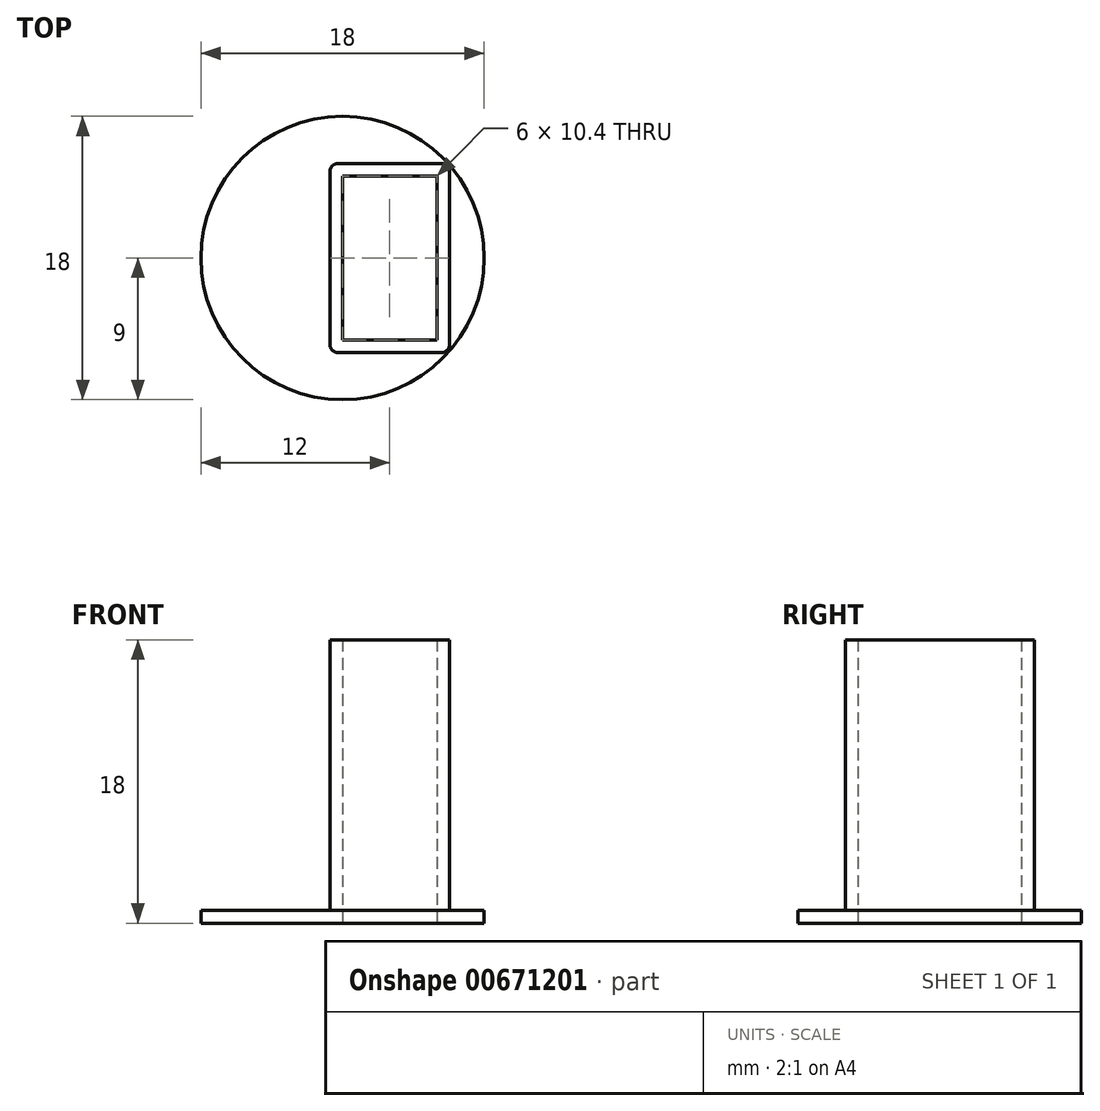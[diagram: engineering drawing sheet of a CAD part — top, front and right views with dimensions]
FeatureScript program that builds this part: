
annotation { "Feature Type Name" : "Feature", "Feature Type Description" : "" }
export const myFeature = defineFeature(function(context is Context, id is Id, definition is map)
    precondition{}
    {
        {
            var Q0;
            Q0=qCreatedBy(makeId("Top.planeOp"),FACE);
            var sketch = newSketch(context, id + "F0", { "sketchPlane" : qUnion([Q0])});
            skCircle(sketch, "E0", {"center": v(0, 0) * mm, "radius": 9 * mm});
            skLineSegment(sketch, "E1.bottom", {"start": v(0, 5.2) * mm, "end": v(6, 5.2) * mm});
            skLineSegment(sketch, "E1.top", {"start": v(0, -5.2) * mm, "end": v(6, -5.2) * mm});
            skLineSegment(sketch, "E1.left", {"start": v(0, 5.2) * mm, "end": v(0, -5.2) * mm});
            skLineSegment(sketch, "E1.right", {"start": v(6, 5.2) * mm, "end": v(6, -5.2) * mm});
            skLineSegment(sketch, "E2.0", {"start": v(6.8, 5.5) * mm, "end": v(6.8, -5.5) * mm});
            skLineSegment(sketch, "E2.1", {"start": v(-0.3, 6) * mm, "end": v(6.3, 6) * mm});
            skLineSegment(sketch, "E2.2", {"start": v(-0.8, 5.5) * mm, "end": v(-0.8, -5.5) * mm});
            skLineSegment(sketch, "E2.3", {"start": v(-0.3, -6) * mm, "end": v(6.3, -6) * mm});
            skPoint(sketch, "E3.visualSharp", {"position": v(-0.8, 6) * mm});
            skArc(sketch, "E3.filletArc", {"start": v(-0.3, 6) * mm, "mid": v(-0.65, 5.85) * mm, "end": v(-0.8, 5.5) * mm});
            skPoint(sketch, "E4.visualSharp", {"position": v(-0.8, -6) * mm});
            skArc(sketch, "E4.filletArc", {"start": v(-0.8, -5.5) * mm, "mid": v(-0.65, -5.85) * mm, "end": v(-0.3, -6) * mm});
            skPoint(sketch, "E5.visualSharp", {"position": v(6.8, -6) * mm});
            skArc(sketch, "E5.filletArc", {"start": v(6.3, -6) * mm, "mid": v(6.65, -5.85) * mm, "end": v(6.8, -5.5) * mm});
            skPoint(sketch, "E6.visualSharp", {"position": v(6.8, 6) * mm});
            skArc(sketch, "E6.filletArc", {"start": v(6.8, 5.5) * mm, "mid": v(6.65, 5.85) * mm, "end": v(6.3, 6) * mm});
            skSolve(sketch);
        }
        {
            var Q0;
            Q0=makeQuery(id+"F0.imprint","IMPRINT",FACE,{"disambiguationData":[TD([[makeQuery(id+"F0.imprint","IMPRINT",EDGE,{"derivedFrom":sQuery(id+"F0.wireOp",EDGE,"E1.bottom")}),1.0]])]});
            extrude(context, id + "F1", {"entities" : qUnion([Q0]), "depth" : 18 * mm, "offsetDistance" : 25 * mm});
        }
        {
            var Q0;
            Q0 = qSketchRegion(id + "F0", true);
            extrude(context, id + "F2", {"entities" : qUnion([Q0]), "operationType" : NewBodyOperationType.ADD, "depth" : 0.8 * mm, "offsetDistance" : 25 * mm});
        }
    });
